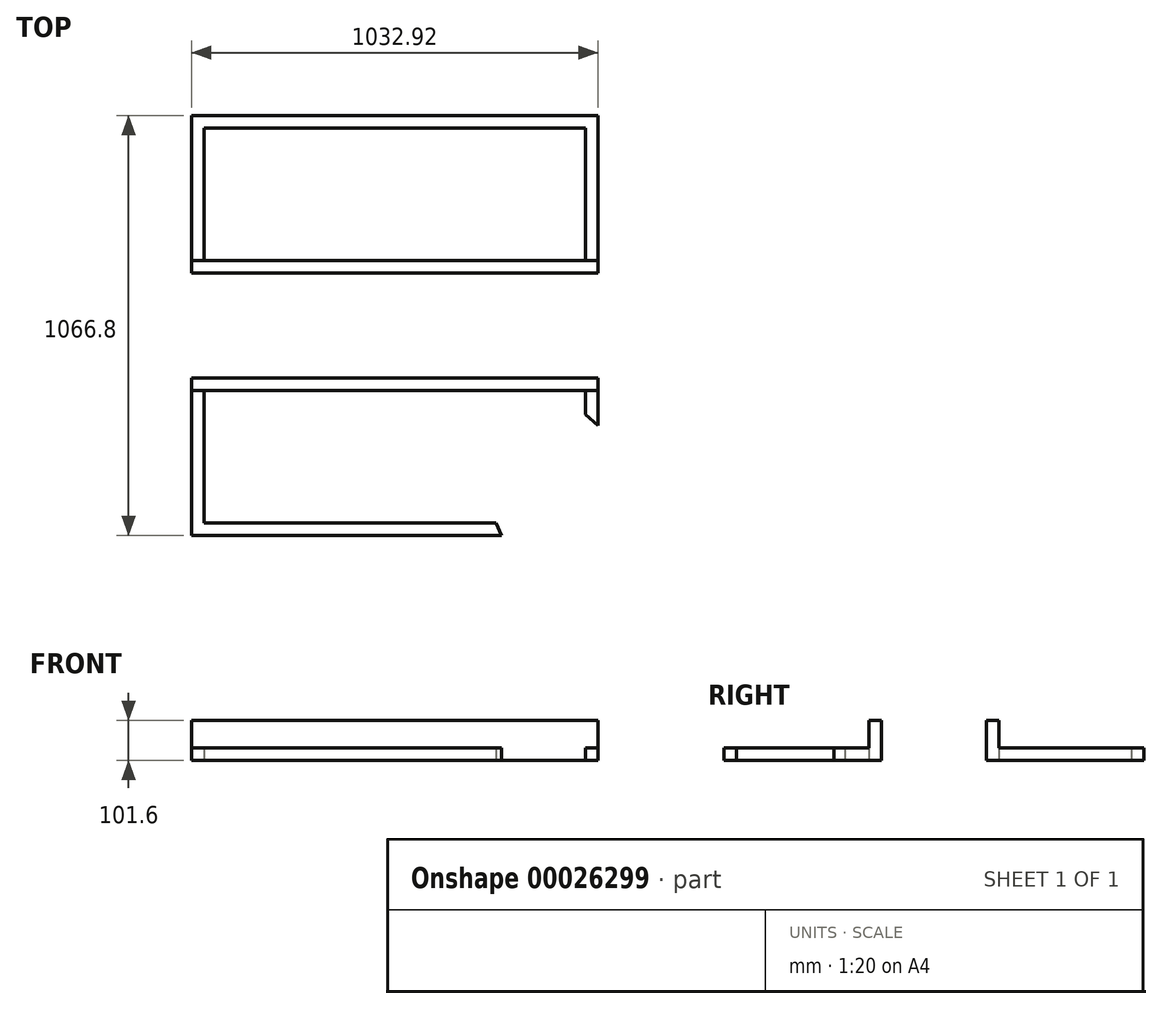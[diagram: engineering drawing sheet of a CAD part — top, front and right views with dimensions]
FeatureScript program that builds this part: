
annotation { "Feature Type Name" : "Feature", "Feature Type Description" : "" }
export const myFeature = defineFeature(function(context is Context, id is Id, definition is map)
    precondition{}
    {
        {
            var Q0;
            Q0=qCreatedBy(makeId("Top.planeOp"),FACE);
            var sketch = newSketch(context, id + "F0", { "sketchPlane" : qUnion([Q0])});
            skArc(sketch, "E0", {"start": v(516.46, 133.35) * mm, "mid": v(0, 533.4) * mm, "end": v(-516.46, 133.35) * mm, "construction": true});
            skLineSegment(sketch, "E1.0", {"start": v(-516.46, 133.35) * mm, "end": v(516.46, 133.35) * mm, "construction": true});
            skLineSegment(sketch, "E2", {"start": v(0, 533.4) * mm, "end": v(516.46, 533.4) * mm});
            skLineSegment(sketch, "E3", {"start": v(516.46, 533.4) * mm, "end": v(516.46, 133.35) * mm});
            skLineSegment(sketch, "E4.MirrorCS", {"start": v(0, 533.4) * mm, "end": v(-516.46, 533.4) * mm});
            skLineSegment(sketch, "E5.MirrorCS", {"start": v(-516.46, 533.4) * mm, "end": v(-516.46, 133.35) * mm});
            skLineSegment(sketch, "E6", {"start": v(-516.46, 133.35) * mm, "end": v(516.46, 133.35) * mm});
            skLineSegment(sketch, "E7.0", {"start": v(-484.71, 501.65) * mm, "end": v(-484.71, 165.1) * mm});
            skLineSegment(sketch, "E7.1", {"start": v(0, 501.65) * mm, "end": v(-484.71, 501.65) * mm});
            skLineSegment(sketch, "E7.2", {"start": v(0, 501.65) * mm, "end": v(484.71, 501.65) * mm});
            skLineSegment(sketch, "E7.3", {"start": v(484.71, 501.65) * mm, "end": v(484.71, 165.1) * mm});
            skLineSegment(sketch, "E7.4", {"start": v(-484.71, 165.1) * mm, "end": v(484.71, 165.1) * mm});
            skSolve(sketch);
        }
        {
            var Q0;
            Q0=makeQuery(id+"F0.imprint","IMPRINT",FACE,{"disambiguationData":[TD([[makeQuery(id+"F0.imprint","IMPRINT",EDGE,{"derivedFrom":sQuery(id+"F0.wireOp",EDGE,"E2")}),-1.0]])]});
            extrude(context, id + "F1", {"entities" : qUnion([Q0]), "depth" : 31.75 * mm});
        }
        {
            var Q0;
            Q0=makeQuery(id+"F1.opExtrude","CAP_FACE",FACE,{"disambiguationData":[OSD([sQuery(id+"F0.wireOp",EDGE,"E2"),sQuery(id+"F0.wireOp",EDGE,"E3"),sQuery(id+"F0.wireOp",EDGE,"E4.MirrorCS"),sQuery(id+"F0.wireOp",EDGE,"E5.MirrorCS"),sQuery(id+"F0.wireOp",EDGE,"E6"),sQuery(id+"F0.wireOp",EDGE,"E7.0"),sQuery(id+"F0.wireOp",EDGE,"E7.1"),sQuery(id+"F0.wireOp",EDGE,"E7.2"),sQuery(id+"F0.wireOp",EDGE,"E7.3"),sQuery(id+"F0.wireOp",EDGE,"E7.4")])],"isStart":false});
            var sketch = newSketch(context, id + "F2", { "sketchPlane" : qUnion([Q0])});
            skLineSegment(sketch, "E8.bottom", {"start": v(-516.46, 165.1) * mm, "end": v(516.46, 165.1) * mm});
            skLineSegment(sketch, "E8.top", {"start": v(-516.46, 133.35) * mm, "end": v(516.46, 133.35) * mm});
            skLineSegment(sketch, "E8.left", {"start": v(-516.46, 165.1) * mm, "end": v(-516.46, 133.35) * mm});
            skLineSegment(sketch, "E8.right", {"start": v(516.46, 165.1) * mm, "end": v(516.46, 133.35) * mm});
            skSolve(sketch);
        }
        {
            var Q0;
            Q0=makeQuery(id+"F2.imprint","IMPRINT",FACE,{"disambiguationData":[TD([[makeQuery(id+"F2.imprint","IMPRINT",EDGE,{"derivedFrom":sQuery(id+"F2.wireOp",EDGE,"E8.top")}),1.0]])]});
            extrude(context, id + "F3", {"entities" : qUnion([Q0]), "operationType" : NewBodyOperationType.ADD, "depth" : 69.85 * mm});
        }
        {
            var Q0;
            Q0=qCreatedBy(makeId("Top.planeOp"),FACE);
            var sketch = newSketch(context, id + "F4", { "sketchPlane" : qUnion([Q0])});
            skArc(sketch, "E9", {"start": v(-516.46, -133.35) * mm, "mid": v(0, -533.4) * mm, "end": v(516.46, -133.35) * mm, "construction": true});
            skLineSegment(sketch, "E10", {"start": v(-533.4, 0) * mm, "end": v(533.4, 0) * mm, "construction": true});
            skLineSegment(sketch, "E11.0", {"start": v(-516.46, -133.35) * mm, "end": v(516.46, -133.35) * mm, "construction": true});
            skLineSegment(sketch, "E12", {"start": v(0, -533.4) * mm, "end": v(516.46, -533.4) * mm, "construction": true});
            skLineSegment(sketch, "E13.bottom", {"start": v(-516.46, -133.35) * mm, "end": v(516.46, -133.35) * mm});
            skLineSegment(sketch, "E13.top", {"start": v(-516.46, -533.4) * mm, "end": v(270.94, -533.4) * mm});
            skLineSegment(sketch, "E13.left", {"start": v(-516.46, -133.35) * mm, "end": v(-516.46, -533.4) * mm});
            skLineSegment(sketch, "E13.right", {"start": v(516.46, -133.35) * mm, "end": v(516.46, -254) * mm});
            skLineSegment(sketch, "E14.0", {"start": v(-484.71, -165.1) * mm, "end": v(-484.71, -501.65) * mm});
            skLineSegment(sketch, "E14.1", {"start": v(-484.71, -165.1) * mm, "end": v(484.71, -165.1) * mm});
            skLineSegment(sketch, "E14.2", {"start": v(484.71, -165.1) * mm, "end": v(484.71, -242.03) * mm});
            skLineSegment(sketch, "E14.3", {"start": v(-484.71, -501.65) * mm, "end": v(256.57, -501.65) * mm});
            skLineSegment(sketch, "E15", {"start": v(-516.46, -533.4) * mm, "end": v(270.94, -533.4) * mm, "construction": true});
            skLineSegment(sketch, "E16", {"start": v(516.46, -533.4) * mm, "end": v(516.46, -254) * mm, "construction": true});
            skLineSegment(sketch, "E17", {"start": v(270.94, -533.4) * mm, "end": v(516.46, -254) * mm});
            skLineSegment(sketch, "E18.0", {"start": v(256.57, -501.65) * mm, "end": v(484.71, -242.03) * mm});
            skLineSegment(sketch, "E19", {"start": v(516.46, -254) * mm, "end": v(437.47, -184.59) * mm});
            skLineSegment(sketch, "E20", {"start": v(484.71, -242.03) * mm, "end": v(516.46, -254) * mm});
            skLineSegment(sketch, "E21", {"start": v(270.94, -533.4) * mm, "end": v(256.57, -501.65) * mm});
            skSolve(sketch);
        }
        {
            var Q0;
            Q0=makeQuery(id+"F4.imprint","IMPRINT",FACE,{"disambiguationData":[TD([[makeQuery(id+"F4.imprint","IMPRINT",EDGE,{"derivedFrom":sQuery(id+"F4.wireOp",EDGE,"E13.bottom")}),-1.0]])]});
            extrude(context, id + "F5", {"entities" : qUnion([Q0]), "depth" : 31.75 * mm});
        }
        {
            var Q0;
            Q0=makeQuery(id+"F5.opExtrude","CAP_FACE",FACE,{"disambiguationData":[OSD([sQuery(id+"F4.wireOp",EDGE,"E13.bottom"),sQuery(id+"F4.wireOp",EDGE,"E13.top"),sQuery(id+"F4.wireOp",EDGE,"E13.left"),sQuery(id+"F4.wireOp",EDGE,"E13.right"),sQuery(id+"F4.wireOp",EDGE,"E14.0"),sQuery(id+"F4.wireOp",EDGE,"E14.1"),sQuery(id+"F4.wireOp",EDGE,"E14.2"),sQuery(id+"F4.wireOp",EDGE,"E14.3")])],"isStart":false});
            var sketch = newSketch(context, id + "F6", { "sketchPlane" : qUnion([Q0])});
            skLineSegment(sketch, "E22.bottom", {"start": v(-516.46, -165.1) * mm, "end": v(516.46, -165.1) * mm});
            skLineSegment(sketch, "E22.top", {"start": v(-516.46, -133.35) * mm, "end": v(516.46, -133.35) * mm});
            skLineSegment(sketch, "E22.left", {"start": v(-516.46, -165.1) * mm, "end": v(-516.46, -133.35) * mm});
            skLineSegment(sketch, "E22.right", {"start": v(516.46, -165.1) * mm, "end": v(516.46, -133.35) * mm});
            skSolve(sketch);
        }
        {
            var Q0;
            Q0=makeQuery(id+"F6.imprint","IMPRINT",FACE,{"disambiguationData":[TD([[makeQuery(id+"F6.imprint","IMPRINT",EDGE,{"derivedFrom":sQuery(id+"F6.wireOp",EDGE,"E22.top")}),-1.0]])]});
            extrude(context, id + "F7", {"entities" : qUnion([Q0]), "operationType" : NewBodyOperationType.ADD, "depth" : 69.85 * mm});
        }
    });
